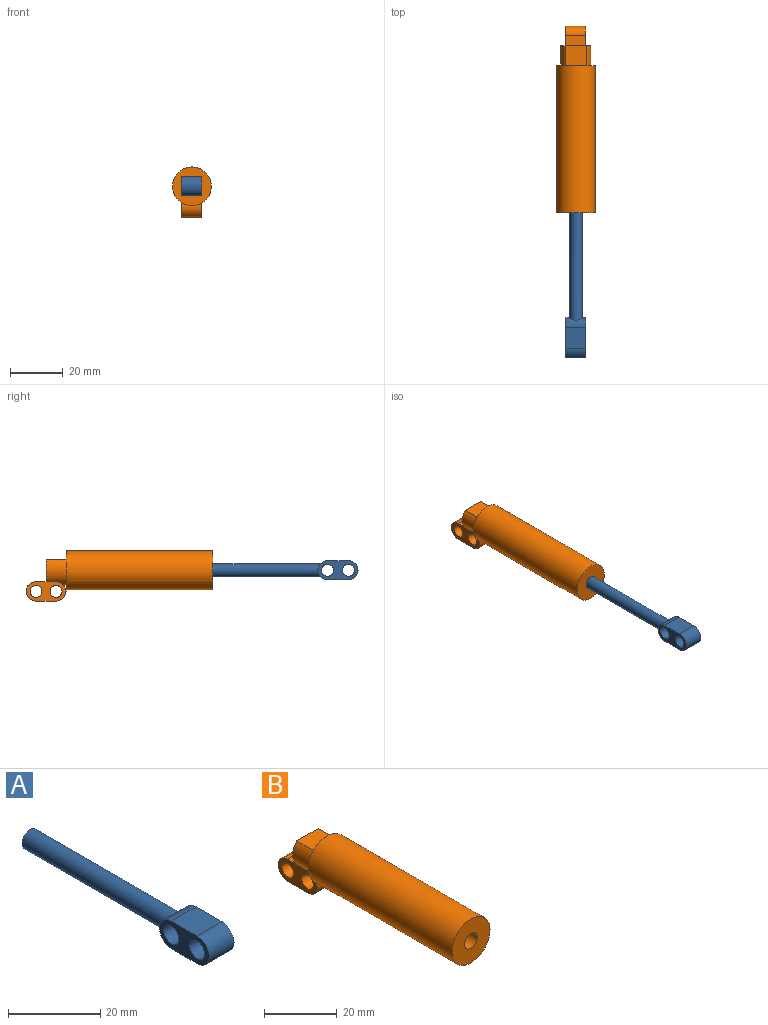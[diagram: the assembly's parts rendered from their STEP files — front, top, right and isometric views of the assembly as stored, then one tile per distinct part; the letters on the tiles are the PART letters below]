
ASSEMBLY  parts=2 mates=1
PART A: 10 faces, bbox 7.6x58.7x7.3 mm
  f0: plane 7.93x7.62mm, normal (0,0,1), area 60.4mm2, adj f1,f5,f6,f7
  f1: cylinder r=3.66mm len=7.62mm, axis (-1,0,0), area 87.6mm2, adj f0,f2,f6,f7
  f2: plane 7.93x7.62mm, normal (0,0,-1), area 60.4mm2, adj f1,f5,f6,f7
  f3: cylinder r=2.29mm len=7.62mm, axis (-1,0,0), area 109.4mm2, adj f6,f7
  f4: cylinder r=2.29mm len=7.62mm, axis (-1,0,0), area 109.4mm2, adj f6,f7
  f5: cylinder r=3.66mm len=7.62mm, axis (-1,0,0), area 67.6mm2, adj f0,f2,f6,f7,f9
  f6: plane 15.24x7.32mm, normal (1,0,0), area 67.2mm2, adj f0,f1,f2,f3,f4,f5
  f7: plane 15.24x7.32mm, normal (-1,0,0), area 67.2mm2, adj f0,f1,f2,f3,f4,f5
  f8: plane 4.88x4.88mm, normal (0,1,0), area 18.7mm2, adj f9
  f9: cylinder r=2.44mm len=44.39mm, axis (0,1,0), area 672.7mm2, adj f5,f8
PART B: 15 faces, bbox 14.8x71.1x19.1 mm
  f0: plane 11.43x8.33mm, normal (0,1,0), area 66.6mm2, adj f3,f4,f5,f9
  f1: cylinder r=7.38mm len=55.88mm, axis (0,1,0), area 2590.7mm2, adj f2,f6
  f2: plane 14.76x14.76mm, normal (0,-1,0), area 151.8mm2, adj f1,f3
  f3: cylinder r=2.48mm len=63.5mm, axis (0,-1,0), area 988.1mm2, adj f0,f2
  f4: cylinder r=5.71mm len=11.43mm, axis (0,1,0), area 153.7mm2, adj f0,f5,f6,f9,f11
  f5: plane 8.29x7.62mm, normal (0,0,1), area 63.1mm2, adj f0,f4,f6
  f6: plane 14.76x14.76mm, normal (0,1,0), area 78.6mm2, adj f1,f4,f5
  f7: plane 7.93x7.62mm, normal (0,0,-1), area 60.4mm2, adj f8,f11,f13,f14
  f8: cylinder r=3.66mm len=7.62mm, axis (-1,0,0), area 87.6mm2, adj f7,f9,f13,f14
  f9: plane 7.93x7.62mm, normal (0,0,1), area 31.4mm2, adj f0,f4,f8,f11,f13,f14
  f10: cylinder r=2.29mm len=7.62mm, axis (-1,0,0), area 109.4mm2, adj f13,f14
  f11: cylinder r=3.66mm len=7.62mm, axis (-1,0,0), area 69mm2, adj f4,f7,f9,f13,f14
  f12: cylinder r=2.29mm len=7.62mm, axis (-1,0,0), area 109.4mm2, adj f13,f14
  f13: plane 15.24x7.32mm, normal (1,0,0), area 67.2mm2, adj f7,f8,f9,f10,f11,f12
  f14: plane 15.24x7.32mm, normal (-1,0,0), area 67.2mm2, adj f7,f8,f9,f10,f11,f12
PLACE A rot(axis=(0,1,0),0deg) t=(-0.09,1.76,-0.12)mm
PLACE B t=(-0.09,1.54,-0.12)mm fixed
MATE cylindrical A.f9 <-> B.f1  axis (0,1,0) through (-0.09,-70.21,-0.12)mm
